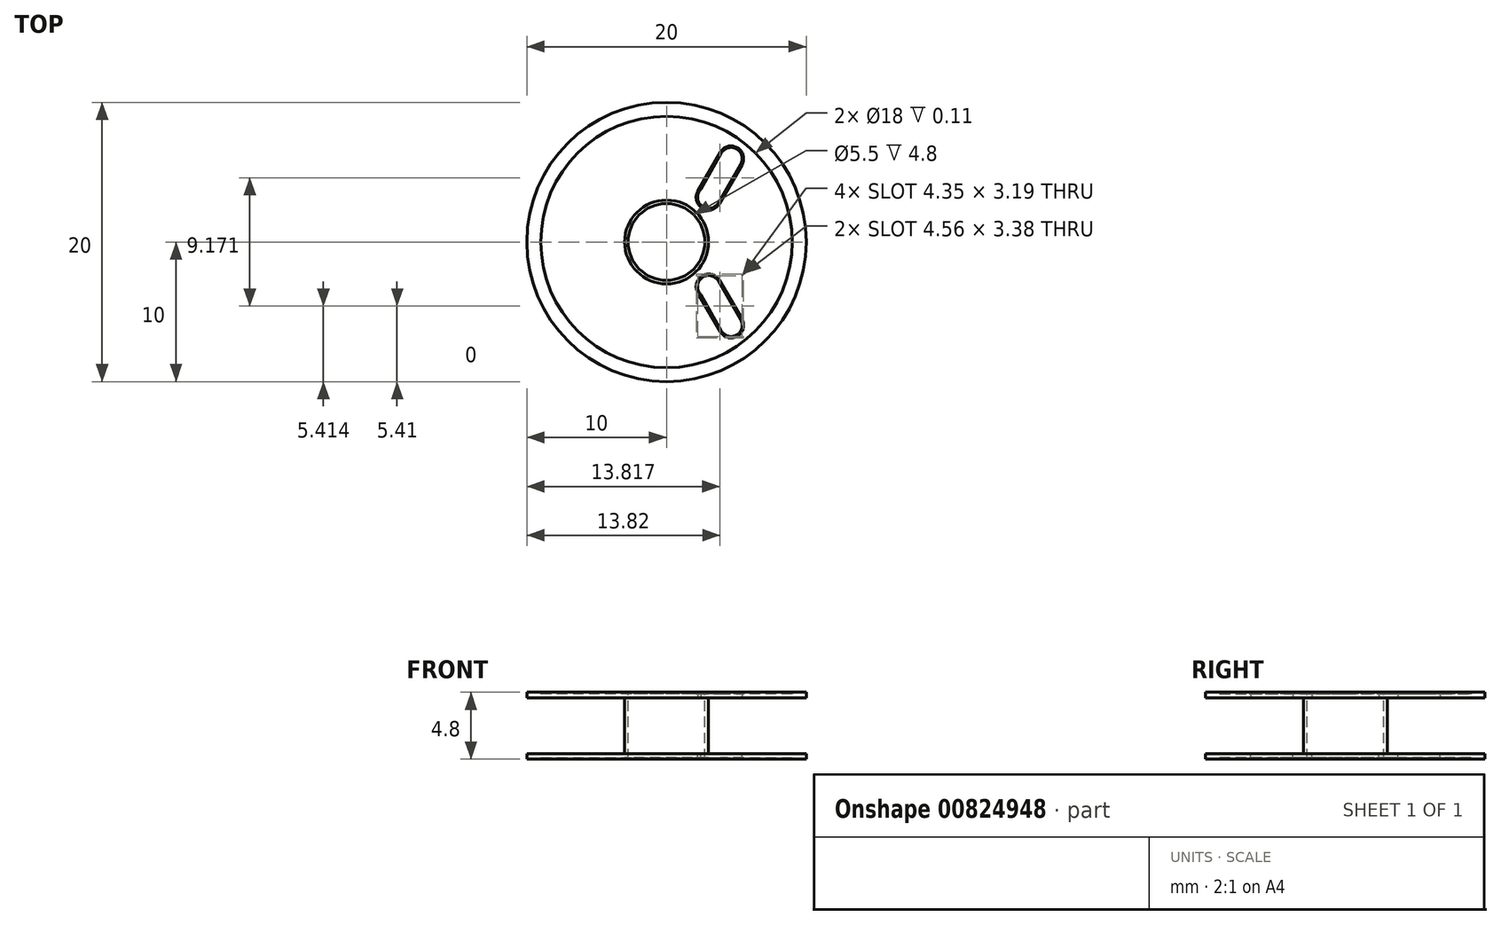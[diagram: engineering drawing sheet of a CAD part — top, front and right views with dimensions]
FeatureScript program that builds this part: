
annotation { "Feature Type Name" : "Feature", "Feature Type Description" : "" }
export const myFeature = defineFeature(function(context is Context, id is Id, definition is map)
    precondition{}
    {
        {
            var Q0;
            Q0=qCreatedBy(makeId("Top.planeOp"),FACE);
            var sketch = newSketch(context, id + "F0", { "sketchPlane" : qUnion([Q0])});
            skCircle(sketch, "E0", {"center": v(0, 0) * mm, "radius": 10 * mm});
            skCircle(sketch, "E1", {"center": v(0, 0) * mm, "radius": 9 * mm});
            skCircle(sketch, "E2", {"center": v(0, 0) * mm, "radius": 3 * mm});
            skCircle(sketch, "E3", {"center": v(0, 0) * mm, "radius": 2.75 * mm});
            skArc(sketch, "E4", {"start": v(5.4, 5.52) * mm, "mid": v(5.07, 6.75) * mm, "end": v(3.84, 6.42) * mm});
            skArc(sketch, "E5", {"start": v(2.24, 3.65) * mm, "mid": v(2.57, 2.42) * mm, "end": v(3.8, 2.75) * mm});
            skArc(sketch, "E6", {"start": v(2.46, 3.77) * mm, "mid": v(2.53, 2.57) * mm, "end": v(3.71, 2.8) * mm});
            skArc(sketch, "E7", {"start": v(5.31, 5.57) * mm, "mid": v(5.02, 6.67) * mm, "end": v(3.92, 6.36) * mm});
            skLineSegment(sketch, "E8", {"start": v(2.24, 3.65) * mm, "end": v(3.84, 6.42) * mm});
            skLineSegment(sketch, "E9", {"start": v(3.8, 2.75) * mm, "end": v(5.4, 5.52) * mm});
            skLineSegment(sketch, "E10", {"start": v(2.24, 3.38) * mm, "end": v(3.92, 6.36) * mm});
            skLineSegment(sketch, "E11", {"start": v(3.71, 2.8) * mm, "end": v(5.4, 5.72) * mm});
            skLineSegment(sketch, "E12.MirrorCS", {"start": v(3.8, -2.75) * mm, "end": v(5.4, -5.52) * mm});
            skLineSegment(sketch, "E13.MirrorCS", {"start": v(3.71, -2.8) * mm, "end": v(5.4, -5.72) * mm});
            skArc(sketch, "E14.MirrorCS", {"start": v(5.4, -5.52) * mm, "mid": v(5.07, -6.75) * mm, "end": v(3.84, -6.42) * mm});
            skArc(sketch, "E15.MirrorCS", {"start": v(5.31, -5.57) * mm, "mid": v(5.02, -6.67) * mm, "end": v(3.92, -6.36) * mm});
            skLineSegment(sketch, "E16.MirrorCS", {"start": v(2.24, -3.38) * mm, "end": v(3.92, -6.36) * mm});
            skLineSegment(sketch, "E17.MirrorCS", {"start": v(2.24, -3.65) * mm, "end": v(3.84, -6.42) * mm});
            skArc(sketch, "E18.MirrorCS", {"start": v(2.46, -3.77) * mm, "mid": v(2.53, -2.57) * mm, "end": v(3.71, -2.8) * mm});
            skArc(sketch, "E19.MirrorCS", {"start": v(2.24, -3.65) * mm, "mid": v(2.57, -2.42) * mm, "end": v(3.8, -2.75) * mm});
            skLineSegment(sketch, "E20.trimOffspring", {"start": v(2.16, -2.94) * mm, "end": v(2.24, -3.04) * mm, "construction": true});
            skSolve(sketch);
        }
        {
            var Q0;
            Q0=makeQuery(id+"F0.imprint","IMPRINT",FACE,{"disambiguationData":[TD([[makeQuery(id+"F0.imprint","IMPRINT",EDGE,{"derivedFrom":sQuery(id+"F0.wireOp",EDGE,"E2")}),1.0]])]});
            var Q1;
            Q1=makeQuery(id+"F0.imprint","IMPRINT",FACE,{"disambiguationData":[TD([[makeQuery(id+"F0.imprint","IMPRINT",EDGE,{"derivedFrom":sQuery(id+"F0.wireOp",EDGE,"E12.MirrorCS")}),-1.0]])]});
            var Q2;
            Q2=makeQuery(id+"F0.imprint","IMPRINT",FACE,{"disambiguationData":[TD([[makeQuery(id+"F0.imprint","IMPRINT",EDGE,{"derivedFrom":sQuery(id+"F0.wireOp",EDGE,"E4")}),1.0]])]});
            var Q3;
            Q3=makeQuery(id+"F0.imprint","IMPRINT",FACE,{"disambiguationData":[TD([[makeQuery(id+"F0.imprint","IMPRINT",EDGE,{"derivedFrom":sQuery(id+"F0.wireOp",EDGE,"E0")}),1.0]])]});
            extrude(context, id + "F1", {"entities" : qUnion([Q0, Q1, Q2, Q3]), "depth" : 0.4 * mm, "offsetDistance" : 25 * mm});
        }
        {
            var Q0;
            Q0=makeQuery(id+"F0.imprint","IMPRINT",FACE,{"disambiguationData":[TD([[makeQuery(id+"F0.imprint","IMPRINT",EDGE,{"derivedFrom":sQuery(id+"F0.wireOp",EDGE,"E1")}),1.0]])]});
            extrude(context, id + "F2", {"entities" : qUnion([Q0]), "depth" : 0.29 * mm, "offsetDistance" : 25 * mm});
        }
        {
            var Q0;
            Q0=makeQuery(id+"F0.imprint","IMPRINT",FACE,{"disambiguationData":[TD([[makeQuery(id+"F0.imprint","IMPRINT",EDGE,{"derivedFrom":sQuery(id+"F0.wireOp",EDGE,"E2")}),1.0]])]});
            extrude(context, id + "F3", {"entities" : qUnion([Q0]), "oppositeDirection" : true, "depth" : 2 * mm, "offsetDistance" : 25 * mm});
        }
        {
            var Q0;
            Q0=makeQuery(id+"F1.opExtrude","SWEPT_BODY",BODY,{"disambiguationData":[OSD([sQuery(id+"F0.wireOp",EDGE,"E0"),sQuery(id+"F0.wireOp",EDGE,"E1")])]});
            var Q1;
            Q1=makeQuery(id+"F2.opExtrude","SWEPT_BODY",BODY,{"disambiguationData":[OSD([sQuery(id+"F0.wireOp",EDGE,"E1"),sQuery(id+"F0.wireOp",EDGE,"E2"),sQuery(id+"F0.wireOp",EDGE,"E4"),sQuery(id+"F0.wireOp",EDGE,"E5"),sQuery(id+"F0.wireOp",EDGE,"E8"),sQuery(id+"F0.wireOp",EDGE,"E9"),sQuery(id+"F0.wireOp",EDGE,"E12.MirrorCS"),sQuery(id+"F0.wireOp",EDGE,"E14.MirrorCS"),sQuery(id+"F0.wireOp",EDGE,"E17.MirrorCS"),sQuery(id+"F0.wireOp",EDGE,"E19.MirrorCS")])]});
            var Q2;
            Q2=makeQuery(id+"F3.opExtrude","SWEPT_BODY",BODY,{"disambiguationData":[OSD([sQuery(id+"F0.wireOp",EDGE,"E2"),sQuery(id+"F0.wireOp",EDGE,"E3")])]});
            var Q3;
            Q3=makeQuery(id+"F1.opExtrude","SWEPT_BODY",BODY,{"disambiguationData":[OSD([sQuery(id+"F0.wireOp",EDGE,"E2"),sQuery(id+"F0.wireOp",EDGE,"E3")])]});
            var Q4;
            Q4=makeQuery(id+"F1.opExtrude","SWEPT_BODY",BODY,{"disambiguationData":[OSD([sQuery(id+"F0.wireOp",EDGE,"E4"),sQuery(id+"F0.wireOp",EDGE,"E5"),sQuery(id+"F0.wireOp",EDGE,"E6"),sQuery(id+"F0.wireOp",EDGE,"E7"),sQuery(id+"F0.wireOp",EDGE,"E8"),sQuery(id+"F0.wireOp",EDGE,"E9"),sQuery(id+"F0.wireOp",EDGE,"E10"),sQuery(id+"F0.wireOp",EDGE,"E11")])]});
            var Q5;
            Q5=makeQuery(id+"F1.opExtrude","SWEPT_BODY",BODY,{"disambiguationData":[OSD([sQuery(id+"F0.wireOp",EDGE,"E12.MirrorCS"),sQuery(id+"F0.wireOp",EDGE,"E13.MirrorCS"),sQuery(id+"F0.wireOp",EDGE,"E14.MirrorCS"),sQuery(id+"F0.wireOp",EDGE,"E15.MirrorCS"),sQuery(id+"F0.wireOp",EDGE,"E16.MirrorCS"),sQuery(id+"F0.wireOp",EDGE,"E17.MirrorCS"),sQuery(id+"F0.wireOp",EDGE,"E18.MirrorCS"),sQuery(id+"F0.wireOp",EDGE,"E19.MirrorCS")])]});
            var Q6;
            Q6=makeQuery(id+"F3.opExtrude","CAP_FACE",FACE,{"disambiguationData":[OSD([sQuery(id+"F0.wireOp",EDGE,"E2"),sQuery(id+"F0.wireOp",EDGE,"E3")])],"isStart":false});
            mirror(context, id + "F4", {"operationType" : NewBodyOperationType.ADD, "entities" : qUnion([Q0, Q1, Q2, Q3, Q4, Q5]), "mirrorPlane" : qUnion([Q6])});
        }
    });
